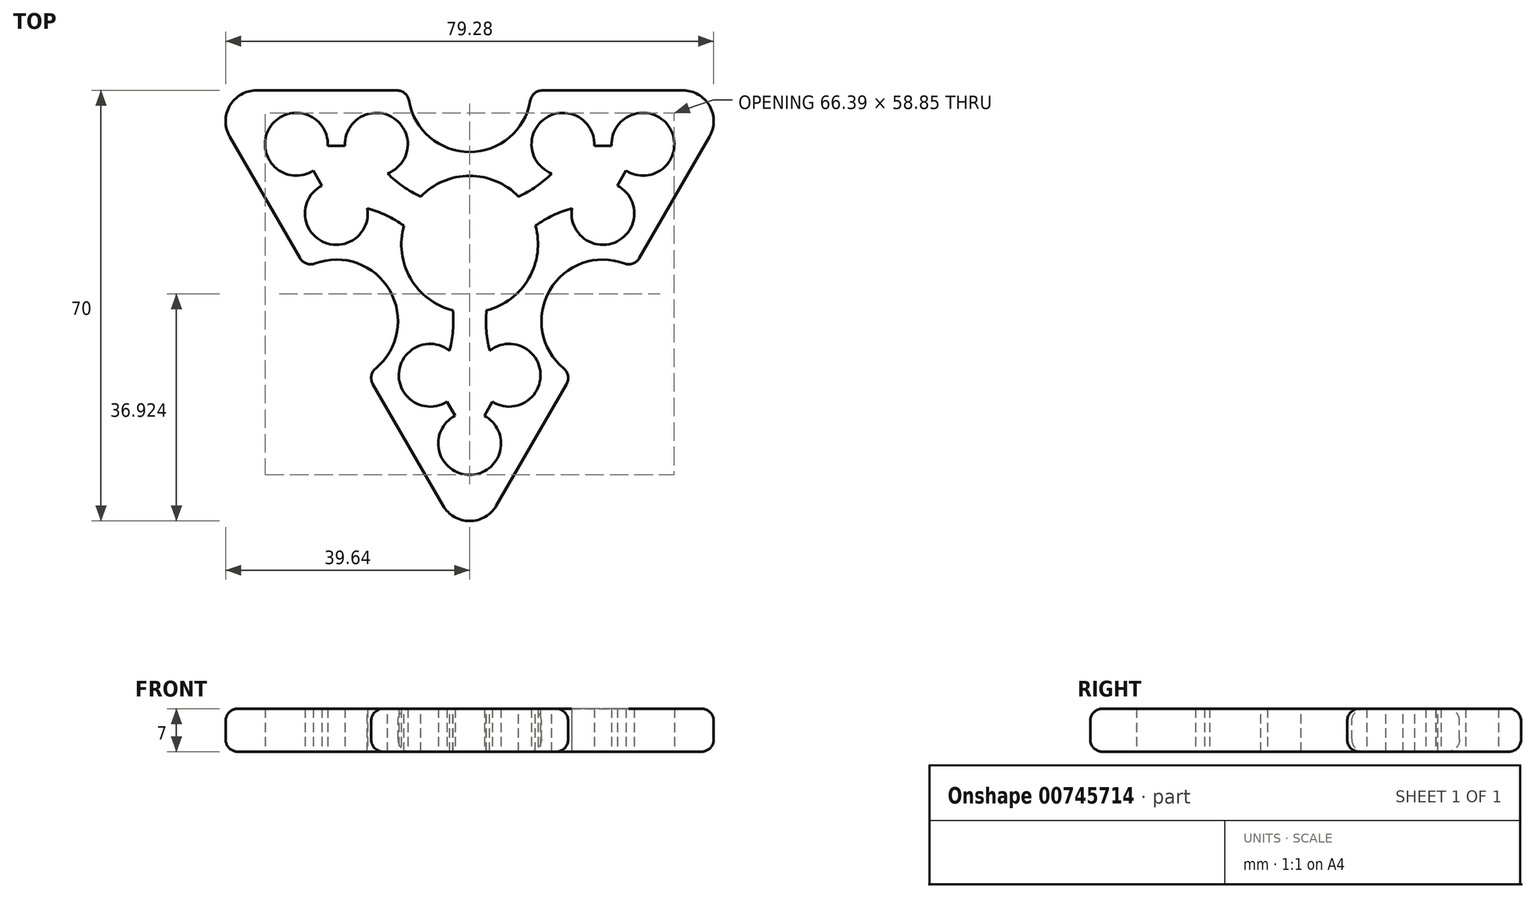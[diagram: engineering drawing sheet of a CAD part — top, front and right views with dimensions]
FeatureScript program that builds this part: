
annotation { "Feature Type Name" : "Feature", "Feature Type Description" : "" }
export const myFeature = defineFeature(function(context is Context, id is Id, definition is map)
    precondition{}
    {
        {
            var Q0;
            Q0=qCreatedBy(makeId("Top.planeOp"),FACE);
            var sketch = newSketch(context, id + "F0", { "sketchPlane" : qUnion([Q0])});
            skCircle(sketch, "E0", {"center": v(0, 0) * mm, "radius": 11.1 * mm});
            skCircle(sketch, "E1", {"center": v(0, -32.4) * mm, "radius": 5.1 * mm});
            skCircle(sketch, "E2.1.0", {"center": v(6.4, -21.3) * mm, "radius": 5.1 * mm});
            skCircle(sketch, "E2.2.0", {"center": v(-6.4, -21.3) * mm, "radius": 5.1 * mm});
            skPoint(sketch, "E2.center", {"position": v(0, -25) * mm});
            skCircle(sketch, "E3.1.1", {"center": v(28.15, 16.25) * mm, "radius": 5.1 * mm});
            skPoint(sketch, "E3.1.2", {"position": v(21.65, 12.5) * mm});
            skCircle(sketch, "E3.1.3", {"center": v(15.16, 16.25) * mm, "radius": 5.1 * mm});
            skCircle(sketch, "E3.1.4", {"center": v(21.65, 5) * mm, "radius": 5.1 * mm});
            skCircle(sketch, "E3.2.1", {"center": v(-28.15, 16.25) * mm, "radius": 5.1 * mm});
            skPoint(sketch, "E3.2.2", {"position": v(-21.65, 12.5) * mm});
            skCircle(sketch, "E3.2.3", {"center": v(-21.65, 5) * mm, "radius": 5.1 * mm});
            skCircle(sketch, "E3.2.4", {"center": v(-15.16, 16.25) * mm, "radius": 5.1 * mm});
            skLineSegment(sketch, "E4", {"start": v(0, 0) * mm, "end": v(0, -37.5) * mm});
            skPoint(sketch, "E5.orphan", {"position": v(0, -45) * mm});
            skPoint(sketch, "E6.orphan", {"position": v(-43.3, 25) * mm});
            skLineSegment(sketch, "E7", {"start": v(0, 0) * mm, "end": v(0, -50) * mm, "construction": true});
            skLineSegment(sketch, "E8", {"start": v(0, 0) * mm, "end": v(-43.3, 25) * mm, "construction": true});
            skLineSegment(sketch, "E9", {"start": v(0, -50) * mm, "end": v(-43.3, 25) * mm});
            skLineSegment(sketch, "E10.1.0", {"start": v(43.3, 25) * mm, "end": v(0, -50) * mm});
            skLineSegment(sketch, "E10.2.0", {"start": v(-43.3, 25) * mm, "end": v(43.3, 25) * mm});
            skSolve(sketch);
        }
        {
            var Q0;
            Q0=makeQuery(id+"F0.imprint","IMPRINT",FACE,{"disambiguationData":[TD([[makeQuery(id+"F0.imprint","IMPRINT",EDGE,{"derivedFrom":sQuery(id+"F0.wireOp",EDGE,"E0")}),-1.0]])]});
            extrude(context, id + "F1", {"entities" : qUnion([Q0]), "depth" : 7 * mm, "offsetDistance" : 25 * mm});
        }
        {
            var Q0;
            Q0=makeQuery(id+"F1.opExtrude","SWEPT_EDGE",EDGE,{"disambiguationData":[OSD([sQuery(id+"F0.wireOp",EDGE,"E9"),sQuery(id+"F0.wireOp",EDGE,"E10.2.0")])]});
            var Q1;
            Q1=makeQuery(id+"F1.opExtrude","SWEPT_EDGE",EDGE,{"disambiguationData":[OSD([sQuery(id+"F0.wireOp",EDGE,"E10.1.0"),sQuery(id+"F0.wireOp",EDGE,"E10.2.0")])]});
            var Q2;
            Q2=makeQuery(id+"F1.opExtrude","SWEPT_EDGE",EDGE,{"disambiguationData":[OSD([sQuery(id+"F0.wireOp",EDGE,"E9"),sQuery(id+"F0.wireOp",EDGE,"E10.1.0")])]});
            fillet(context, id + "F2", {"entities" : qUnion([Q0, Q1, Q2]), "radius" : 5 * mm, "tangentPropagation" : true, "allowEdgeOverflow" : false});
        }
        {
            var Q0;
            Q0=makeQuery(id+"F1.opExtrude","CAP_FACE",FACE,{"disambiguationData":[OSD([sQuery(id+"F0.wireOp",EDGE,"E0"),sQuery(id+"F0.wireOp",EDGE,"E1"),sQuery(id+"F0.wireOp",EDGE,"E2.1.0"),sQuery(id+"F0.wireOp",EDGE,"E2.2.0"),sQuery(id+"F0.wireOp",EDGE,"E3.1.1"),sQuery(id+"F0.wireOp",EDGE,"E3.1.3"),sQuery(id+"F0.wireOp",EDGE,"E3.1.4"),sQuery(id+"F0.wireOp",EDGE,"E3.2.1"),sQuery(id+"F0.wireOp",EDGE,"E3.2.3"),sQuery(id+"F0.wireOp",EDGE,"E3.2.4"),sQuery(id+"F0.wireOp",EDGE,"E9"),sQuery(id+"F0.wireOp",EDGE,"E10.1.0"),sQuery(id+"F0.wireOp",EDGE,"E10.2.0")])],"isStart":false});
            var sketch = newSketch(context, id + "F3", { "sketchPlane" : qUnion([Q0])});
            skCircle(sketch, "E11", {"center": v(0, 25) * mm, "radius": 10 * mm});
            skCircle(sketch, "E12.1.0", {"center": v(-21.65, -12.5) * mm, "radius": 10 * mm});
            skCircle(sketch, "E12.2.0", {"center": v(21.65, -12.5) * mm, "radius": 10 * mm});
            skPoint(sketch, "E12.center", {"position": v(0, 0) * mm});
            skSolve(sketch);
        }
        {
            var Q0;
            {var subQ0=sQuery(id+"F3.wireOp",EDGE,"E11");var subQ1=makeQuery(id+"F1.opExtrude","CAP_EDGE",EDGE,{"disambiguationData":[OSD([sQuery(id+"F0.wireOp",EDGE,"E10.2.0")])],"isStart":false});var subQ2=makeQuery(id+"F3.imprint","INTERSECT",VERTEX,{"disambiguationData":[OD(0.0)],"derivedFrom":[subQ1,subQ0]});Q0=makeQuery(id+"F3.imprint","IMPRINT",FACE,{"disambiguationData":[TD([[makeQuery(id+"F3.imprint","IMPRINT",EDGE,{"disambiguationData":[TD([[subQ2,-1.0]])],"derivedFrom":subQ0}),1.0]])]});}
            var Q1;
            {var subQ0=sQuery(id+"F3.wireOp",EDGE,"E12.1.0");var subQ1=makeQuery(id+"F1.opExtrude","CAP_EDGE",EDGE,{"disambiguationData":[OSD([sQuery(id+"F0.wireOp",EDGE,"E9")])],"isStart":false});var subQ2=makeQuery(id+"F3.imprint","INTERSECT",VERTEX,{"disambiguationData":[OD(0.0)],"derivedFrom":[subQ1,subQ0]});Q1=makeQuery(id+"F3.imprint","IMPRINT",FACE,{"disambiguationData":[TD([[makeQuery(id+"F3.imprint","IMPRINT",EDGE,{"disambiguationData":[TD([[subQ2,-1.0]])],"derivedFrom":subQ0}),1.0]])]});}
            var Q2;
            {var subQ0=sQuery(id+"F3.wireOp",EDGE,"E12.2.0");var subQ1=makeQuery(id+"F1.opExtrude","CAP_EDGE",EDGE,{"disambiguationData":[OSD([sQuery(id+"F0.wireOp",EDGE,"E10.1.0")])],"isStart":false});var subQ2=makeQuery(id+"F3.imprint","INTERSECT",VERTEX,{"disambiguationData":[OD(0.0)],"derivedFrom":[subQ1,subQ0]});Q2=makeQuery(id+"F3.imprint","IMPRINT",FACE,{"disambiguationData":[TD([[makeQuery(id+"F3.imprint","IMPRINT",EDGE,{"disambiguationData":[TD([[subQ2,1.0]])],"derivedFrom":subQ0}),1.0]])]});}
            extrude(context, id + "F4", {"entities" : qUnion([Q0, Q1, Q2]), "operationType" : NewBodyOperationType.REMOVE, "oppositeDirection" : true, "depth" : 25 * mm, "offsetDistance" : 25 * mm});
        }
        {
            var Q0;
            {var subQ0=sQuery(id+"F0.wireOp",EDGE,"E10.1.0");var subQ1=sQuery(id+"F0.wireOp",EDGE,"E9");Q0=makeQuery(id+"F4.boolean.opBoolean","SPLIT",EDGE,{"disambiguationData":[TD([makeQuery(id+"F2.opFillet","BLEND_FACE",FACE,{"disambiguationData":[OSD([subQ1,subQ0])]})])],"derivedFrom":makeQuery(id+"F1.opExtrude","CAP_EDGE",EDGE,{"disambiguationData":[OSD([subQ0])],"isStart":true})});}
            var Q1;
            {var subQ0=sQuery(id+"F0.wireOp",EDGE,"E10.2.0");var subQ1=sQuery(id+"F0.wireOp",EDGE,"E10.1.0");Q1=makeQuery(id+"F4.boolean.opBoolean","SPLIT",EDGE,{"disambiguationData":[TD([makeQuery(id+"F2.opFillet","BLEND_FACE",FACE,{"disambiguationData":[OSD([subQ1,subQ0])]})])],"derivedFrom":makeQuery(id+"F1.opExtrude","CAP_EDGE",EDGE,{"disambiguationData":[OSD([subQ1])],"isStart":true})});}
            var Q2;
            {var subQ0=sQuery(id+"F0.wireOp",EDGE,"E10.2.0");var subQ1=sQuery(id+"F0.wireOp",EDGE,"E9");Q2=makeQuery(id+"F4.boolean.opBoolean","SPLIT",EDGE,{"disambiguationData":[TD([makeQuery(id+"F2.opFillet","BLEND_FACE",FACE,{"disambiguationData":[OSD([subQ1,subQ0])]})])],"derivedFrom":makeQuery(id+"F1.opExtrude","CAP_EDGE",EDGE,{"disambiguationData":[OSD([subQ0])],"isStart":true})});}
            var Q3;
            {var subQ0=sQuery(id+"F0.wireOp",EDGE,"E10.2.0");var subQ1=sQuery(id+"F0.wireOp",EDGE,"E9");Q3=makeQuery(id+"F2.opFillet","BLEND_EDGE",EDGE,{"blendedFrom":[makeQuery(id+"F1.opExtrude","SWEPT_EDGE",EDGE,{"disambiguationData":[OSD([subQ1,subQ0])]}),makeQuery(id+"F1.opExtrude","CAP_FACE",FACE,{"disambiguationData":[OSD([sQuery(id+"F0.wireOp",EDGE,"E0"),sQuery(id+"F0.wireOp",EDGE,"E1"),sQuery(id+"F0.wireOp",EDGE,"E2.1.0"),sQuery(id+"F0.wireOp",EDGE,"E2.2.0"),sQuery(id+"F0.wireOp",EDGE,"E3.1.1"),sQuery(id+"F0.wireOp",EDGE,"E3.1.3"),sQuery(id+"F0.wireOp",EDGE,"E3.1.4"),sQuery(id+"F0.wireOp",EDGE,"E3.2.1"),sQuery(id+"F0.wireOp",EDGE,"E3.2.3"),sQuery(id+"F0.wireOp",EDGE,"E3.2.4"),subQ1,sQuery(id+"F0.wireOp",EDGE,"E10.1.0"),subQ0])],"isStart":false})],"blendedInto":[makeQuery(id+"F1.opExtrude","CAP_FACE",FACE,{"disambiguationData":[OSD([sQuery(id+"F0.wireOp",EDGE,"E0"),sQuery(id+"F0.wireOp",EDGE,"E1"),sQuery(id+"F0.wireOp",EDGE,"E2.1.0"),sQuery(id+"F0.wireOp",EDGE,"E2.2.0"),sQuery(id+"F0.wireOp",EDGE,"E3.1.1"),sQuery(id+"F0.wireOp",EDGE,"E3.1.3"),sQuery(id+"F0.wireOp",EDGE,"E3.1.4"),sQuery(id+"F0.wireOp",EDGE,"E3.2.1"),sQuery(id+"F0.wireOp",EDGE,"E3.2.3"),sQuery(id+"F0.wireOp",EDGE,"E3.2.4"),subQ1,sQuery(id+"F0.wireOp",EDGE,"E10.1.0"),subQ0])],"isStart":false})]});}
            var Q4;
            {var subQ0=sQuery(id+"F0.wireOp",EDGE,"E10.2.0");var subQ1=sQuery(id+"F0.wireOp",EDGE,"E10.1.0");Q4=makeQuery(id+"F2.opFillet","BLEND_EDGE",EDGE,{"blendedFrom":[makeQuery(id+"F1.opExtrude","SWEPT_EDGE",EDGE,{"disambiguationData":[OSD([subQ1,subQ0])]}),makeQuery(id+"F1.opExtrude","CAP_FACE",FACE,{"disambiguationData":[OSD([sQuery(id+"F0.wireOp",EDGE,"E0"),sQuery(id+"F0.wireOp",EDGE,"E1"),sQuery(id+"F0.wireOp",EDGE,"E2.1.0"),sQuery(id+"F0.wireOp",EDGE,"E2.2.0"),sQuery(id+"F0.wireOp",EDGE,"E3.1.1"),sQuery(id+"F0.wireOp",EDGE,"E3.1.3"),sQuery(id+"F0.wireOp",EDGE,"E3.1.4"),sQuery(id+"F0.wireOp",EDGE,"E3.2.1"),sQuery(id+"F0.wireOp",EDGE,"E3.2.3"),sQuery(id+"F0.wireOp",EDGE,"E3.2.4"),sQuery(id+"F0.wireOp",EDGE,"E9"),subQ1,subQ0])],"isStart":false})],"blendedInto":[makeQuery(id+"F1.opExtrude","CAP_FACE",FACE,{"disambiguationData":[OSD([sQuery(id+"F0.wireOp",EDGE,"E0"),sQuery(id+"F0.wireOp",EDGE,"E1"),sQuery(id+"F0.wireOp",EDGE,"E2.1.0"),sQuery(id+"F0.wireOp",EDGE,"E2.2.0"),sQuery(id+"F0.wireOp",EDGE,"E3.1.1"),sQuery(id+"F0.wireOp",EDGE,"E3.1.3"),sQuery(id+"F0.wireOp",EDGE,"E3.1.4"),sQuery(id+"F0.wireOp",EDGE,"E3.2.1"),sQuery(id+"F0.wireOp",EDGE,"E3.2.3"),sQuery(id+"F0.wireOp",EDGE,"E3.2.4"),sQuery(id+"F0.wireOp",EDGE,"E9"),subQ1,subQ0])],"isStart":false})]});}
            var Q5;
            {var subQ0=sQuery(id+"F0.wireOp",EDGE,"E10.1.0");var subQ1=sQuery(id+"F0.wireOp",EDGE,"E9");Q5=makeQuery(id+"F2.opFillet","BLEND_EDGE",EDGE,{"blendedFrom":[makeQuery(id+"F1.opExtrude","SWEPT_EDGE",EDGE,{"disambiguationData":[OSD([subQ1,subQ0])]}),makeQuery(id+"F1.opExtrude","CAP_FACE",FACE,{"disambiguationData":[OSD([sQuery(id+"F0.wireOp",EDGE,"E0"),sQuery(id+"F0.wireOp",EDGE,"E1"),sQuery(id+"F0.wireOp",EDGE,"E2.1.0"),sQuery(id+"F0.wireOp",EDGE,"E2.2.0"),sQuery(id+"F0.wireOp",EDGE,"E3.1.1"),sQuery(id+"F0.wireOp",EDGE,"E3.1.3"),sQuery(id+"F0.wireOp",EDGE,"E3.1.4"),sQuery(id+"F0.wireOp",EDGE,"E3.2.1"),sQuery(id+"F0.wireOp",EDGE,"E3.2.3"),sQuery(id+"F0.wireOp",EDGE,"E3.2.4"),subQ1,subQ0,sQuery(id+"F0.wireOp",EDGE,"E10.2.0")])],"isStart":false})],"blendedInto":[makeQuery(id+"F1.opExtrude","CAP_FACE",FACE,{"disambiguationData":[OSD([sQuery(id+"F0.wireOp",EDGE,"E0"),sQuery(id+"F0.wireOp",EDGE,"E1"),sQuery(id+"F0.wireOp",EDGE,"E2.1.0"),sQuery(id+"F0.wireOp",EDGE,"E2.2.0"),sQuery(id+"F0.wireOp",EDGE,"E3.1.1"),sQuery(id+"F0.wireOp",EDGE,"E3.1.3"),sQuery(id+"F0.wireOp",EDGE,"E3.1.4"),sQuery(id+"F0.wireOp",EDGE,"E3.2.1"),sQuery(id+"F0.wireOp",EDGE,"E3.2.3"),sQuery(id+"F0.wireOp",EDGE,"E3.2.4"),subQ1,subQ0,sQuery(id+"F0.wireOp",EDGE,"E10.2.0")])],"isStart":false})]});}
            fillet(context, id + "F5", {"entities" : qUnion([Q0, Q1, Q2, Q3, Q4, Q5]), "radius" : 2 * mm, "tangentPropagation" : true, "allowEdgeOverflow" : false});
        }
        {
            var Q0;
            Q0=makeQuery(id+"F4.boolean.opBoolean","INTERSECT",EDGE,{"derivedFrom":[makeQuery(id+"F1.opExtrude","CAP_FACE",FACE,{"disambiguationData":[OSD([sQuery(id+"F0.wireOp",EDGE,"E0"),sQuery(id+"F0.wireOp",EDGE,"E1"),sQuery(id+"F0.wireOp",EDGE,"E2.1.0"),sQuery(id+"F0.wireOp",EDGE,"E2.2.0"),sQuery(id+"F0.wireOp",EDGE,"E3.1.1"),sQuery(id+"F0.wireOp",EDGE,"E3.1.3"),sQuery(id+"F0.wireOp",EDGE,"E3.1.4"),sQuery(id+"F0.wireOp",EDGE,"E3.2.1"),sQuery(id+"F0.wireOp",EDGE,"E3.2.3"),sQuery(id+"F0.wireOp",EDGE,"E3.2.4"),sQuery(id+"F0.wireOp",EDGE,"E9"),sQuery(id+"F0.wireOp",EDGE,"E10.1.0"),sQuery(id+"F0.wireOp",EDGE,"E10.2.0")])],"isStart":true}),makeQuery(id+"F4.opExtrude","SWEPT_FACE",FACE,{"disambiguationData":[OSD([sQuery(id+"F3.wireOp",EDGE,"E12.2.0")])]})]});
            var Q1;
            Q1=makeQuery(id+"F4.boolean.opBoolean","INTERSECT",EDGE,{"derivedFrom":[makeQuery(id+"F1.opExtrude","CAP_FACE",FACE,{"disambiguationData":[OSD([sQuery(id+"F0.wireOp",EDGE,"E0"),sQuery(id+"F0.wireOp",EDGE,"E1"),sQuery(id+"F0.wireOp",EDGE,"E2.1.0"),sQuery(id+"F0.wireOp",EDGE,"E2.2.0"),sQuery(id+"F0.wireOp",EDGE,"E3.1.1"),sQuery(id+"F0.wireOp",EDGE,"E3.1.3"),sQuery(id+"F0.wireOp",EDGE,"E3.1.4"),sQuery(id+"F0.wireOp",EDGE,"E3.2.1"),sQuery(id+"F0.wireOp",EDGE,"E3.2.3"),sQuery(id+"F0.wireOp",EDGE,"E3.2.4"),sQuery(id+"F0.wireOp",EDGE,"E9"),sQuery(id+"F0.wireOp",EDGE,"E10.1.0"),sQuery(id+"F0.wireOp",EDGE,"E10.2.0")])],"isStart":true}),makeQuery(id+"F4.opExtrude","SWEPT_FACE",FACE,{"disambiguationData":[OSD([sQuery(id+"F3.wireOp",EDGE,"E12.1.0")])]})]});
            var Q2;
            Q2=makeQuery(id+"F4.boolean.opBoolean","INTERSECT",EDGE,{"derivedFrom":[makeQuery(id+"F1.opExtrude","CAP_FACE",FACE,{"disambiguationData":[OSD([sQuery(id+"F0.wireOp",EDGE,"E0"),sQuery(id+"F0.wireOp",EDGE,"E1"),sQuery(id+"F0.wireOp",EDGE,"E2.1.0"),sQuery(id+"F0.wireOp",EDGE,"E2.2.0"),sQuery(id+"F0.wireOp",EDGE,"E3.1.1"),sQuery(id+"F0.wireOp",EDGE,"E3.1.3"),sQuery(id+"F0.wireOp",EDGE,"E3.1.4"),sQuery(id+"F0.wireOp",EDGE,"E3.2.1"),sQuery(id+"F0.wireOp",EDGE,"E3.2.3"),sQuery(id+"F0.wireOp",EDGE,"E3.2.4"),sQuery(id+"F0.wireOp",EDGE,"E9"),sQuery(id+"F0.wireOp",EDGE,"E10.1.0"),sQuery(id+"F0.wireOp",EDGE,"E10.2.0")])],"isStart":true}),makeQuery(id+"F4.opExtrude","SWEPT_FACE",FACE,{"disambiguationData":[OSD([sQuery(id+"F3.wireOp",EDGE,"E11")])]})]});
            fillet(context, id + "F6", {"entities" : qUnion([Q0, Q1, Q2]), "radius" : 2 * mm, "tangentPropagation" : true, "allowEdgeOverflow" : false});
        }
        {
            var Q0;
            Q0=makeQuery(id+"F1.opExtrude","CAP_FACE",FACE,{"disambiguationData":[OSD([sQuery(id+"F0.wireOp",EDGE,"E0"),sQuery(id+"F0.wireOp",EDGE,"E1"),sQuery(id+"F0.wireOp",EDGE,"E2.1.0"),sQuery(id+"F0.wireOp",EDGE,"E2.2.0"),sQuery(id+"F0.wireOp",EDGE,"E3.1.1"),sQuery(id+"F0.wireOp",EDGE,"E3.1.3"),sQuery(id+"F0.wireOp",EDGE,"E3.1.4"),sQuery(id+"F0.wireOp",EDGE,"E3.2.1"),sQuery(id+"F0.wireOp",EDGE,"E3.2.3"),sQuery(id+"F0.wireOp",EDGE,"E3.2.4"),sQuery(id+"F0.wireOp",EDGE,"E9"),sQuery(id+"F0.wireOp",EDGE,"E10.1.0"),sQuery(id+"F0.wireOp",EDGE,"E10.2.0")])],"isStart":false});
            var sketch = newSketch(context, id + "F7", { "sketchPlane" : qUnion([Q0])});
            skArc(sketch, "E13.0", {"start": v(16.73, 16) * mm, "mid": v(0, 6) * mm, "end": v(-16.73, 16) * mm});
            skLineSegment(sketch, "E13.1", {"start": v(27.71, 16) * mm, "end": v(16.73, 16) * mm});
            skLineSegment(sketch, "E13.2", {"start": v(-16.73, 16) * mm, "end": v(-27.71, 16) * mm});
            skLineSegment(sketch, "E13.3", {"start": v(22.22, 6.5) * mm, "end": v(27.71, 16) * mm});
            skArc(sketch, "E13.4", {"start": v(5.49, -22.5) * mm, "mid": v(5.2, -3) * mm, "end": v(22.22, 6.5) * mm});
            skLineSegment(sketch, "E13.5", {"start": v(-27.71, 16) * mm, "end": v(-22.22, 6.5) * mm});
            skArc(sketch, "E13.6", {"start": v(-22.22, 6.5) * mm, "mid": v(-5.2, -3) * mm, "end": v(-5.49, -22.5) * mm});
            skLineSegment(sketch, "E13.7", {"start": v(-5.49, -22.5) * mm, "end": v(0, -32) * mm});
            skLineSegment(sketch, "E13.8", {"start": v(0, -32) * mm, "end": v(5.49, -22.5) * mm});
            skSolve(sketch);
        }
        {
            var Q0;
            Q0 = qSketchRegion(id + "F7", true);
            extrude(context, id + "F8", {"entities" : qUnion([Q0]), "operationType" : NewBodyOperationType.REMOVE, "oppositeDirection" : true, "depth" : 25 * mm, "offsetDistance" : 25 * mm});
        }
    });
